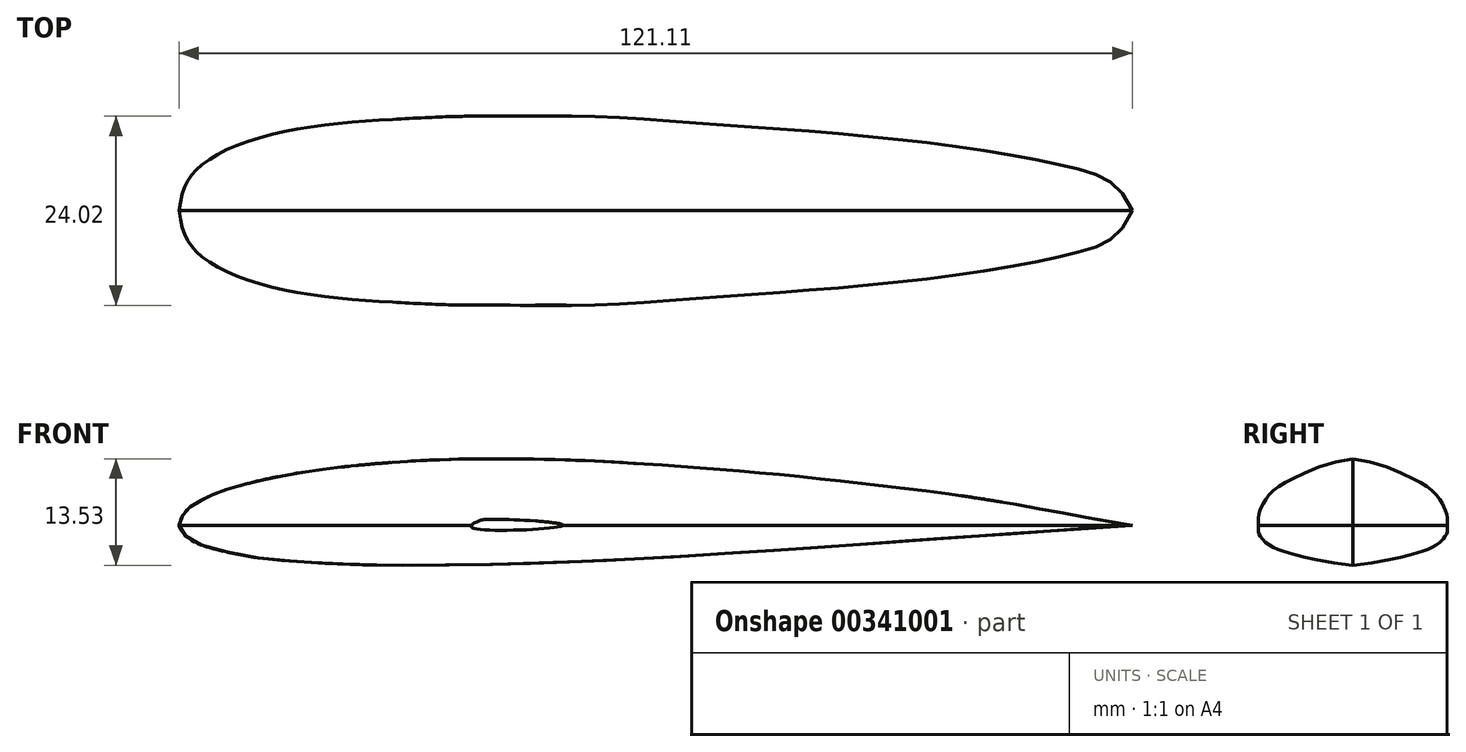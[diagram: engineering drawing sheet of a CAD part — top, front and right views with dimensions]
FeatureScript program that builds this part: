
annotation { "Feature Type Name" : "Feature", "Feature Type Description" : "" }
export const myFeature = defineFeature(function(context is Context, id is Id, definition is map)
    precondition{}
    {
        {
            var Q0;
            Q0=qCreatedBy(makeId("Front.planeOp"),FACE);
            var sketch = newSketch(context, id + "F0", { "sketchPlane" : qUnion([Q0])});
            skFitSpline(sketch, "E0", {"points": [v(-109.58, 0) * mm, v(-108.84, 1.66) * mm, v(-106.74, 3.18) * mm, v(-103.8, 4.43) * mm, v(-98.15, 5.93) * mm, v(-91.38, 7.1) * mm, v(-82.4, 7.99) * mm, v(-72.78, 8.41) * mm, v(-60.7, 8.3) * mm, v(-50.48, 7.79) * mm, v(-37.9, 6.86) * mm, v(-23.66, 5.4) * mm, v(-6.97, 3.25) * mm, v(11.53, 0) * mm], "startDerivative": vector(15.02, 46.78) * mm, "endDerivative": vector(165.18, -26.76) * mm});
            skLineSegment(sketch, "E1", {"start": v(11.53, 0) * mm, "end": v(11.53, 0) * mm});
            skFitSpline(sketch, "E2", {"points": [v(-109.58, 0) * mm, v(-109.4, -0.48) * mm, v(-108.4, -1.65) * mm, v(-106.45, -2.6) * mm, v(-101.35, -3.84) * mm, v(-95.03, -4.6) * mm, v(-86.91, -5) * mm, v(-76.49, -5.08) * mm, v(-63.19, -4.78) * mm, v(-51.7, -4.3) * mm, v(-35.91, -3.33) * mm, v(-24.18, -2.5) * mm, v(-10.17, -1.52) * mm, v(11.53, 0) * mm], "startDerivative": vector(4.26, -26.1) * mm, "endDerivative": vector(181.81, 12.76) * mm});
            skPoint(sketch, "E3", {"position": v(-109.56, 50.72) * mm});
            skSolve(sketch);
        }
        {
            var Q0;
            Q0=qCreatedBy(makeId("Front.planeOp"),FACE);
            cPlane(context, id + "F1", {"entities" : qUnion([Q0]), "cplaneType" : CPlaneType.OFFSET, "offset" : 12 * mm, "width" : 150 * mm, "height" : 150 * mm});
        }
        {
            var Q0;
            Q0=qCreatedBy(id+"F1.planeOp",FACE);
            var sketch = newSketch(context, id + "F2", { "sketchPlane" : qUnion([Q0])});
            skFitSpline(sketch, "E4", {"points": [v(-70.05, 0.77) * mm, v(-71.57, 0.5) * mm, v(-72.41, 0) * mm, v(-71.78, -0.48) * mm, v(-60.78, 0) * mm, v(-70.05, 0.77) * mm]});
            skPoint(sketch, "E5", {"position": v(-67.2, 0.7) * mm});
            skPoint(sketch, "E6", {"position": v(-64.3, 0.53) * mm});
            skPoint(sketch, "E7", {"position": v(-69.51, -0.64) * mm});
            skPoint(sketch, "E8", {"position": v(-66.72, -0.62) * mm});
            skPoint(sketch, "E9", {"position": v(-63.78, -0.47) * mm});
            skPoint(sketch, "E10", {"position": v(-61.75, -0.26) * mm});
            skPoint(sketch, "E11", {"position": v(-61.99, 0.32) * mm});
            skPoint(sketch, "E12", {"position": v(-60.82, 0.06) * mm});
            skPoint(sketch, "E13", {"position": v(-60.82, -0.04) * mm});
            skSolve(sketch);
        }
        {
            var Q0;
            Q0=qCreatedBy(makeId("Top.planeOp"),FACE);
            var sketch = newSketch(context, id + "F3", { "sketchPlane" : qUnion([Q0])});
            skFitSpline(sketch, "E14", {"points": [v(-109.58, 0) * mm, v(-107.55, -5.01) * mm, v(-98.59, -9.5) * mm, v(-81.02, -11.7) * mm, v(-72.41, -12) * mm], "startDerivative": vector(6.08, -37.14) * mm, "endDerivative": vector(19.3, 0.26) * mm});
            skFitSpline(sketch, "E15", {"points": [v(11.53, 0) * mm, v(4.5, -5.32) * mm, v(-15.68, -8.78) * mm, v(-41.53, -11) * mm, v(-60.78, -12) * mm], "startDerivative": vector(-25.52, -62.57) * mm, "endDerivative": vector(-69.24, 0.83) * mm});
            skSolve(sketch);
        }
        {
            var Q0;
            Q0=makeQuery(id+"F0.imprint","IMPRINT",FACE,{"disambiguationData":[TD([[makeQuery(id+"F0.imprint","IMPRINT",EDGE,{"derivedFrom":sQuery(id+"F0.wireOp",EDGE,"E0")}),-1.0]])]});
            var Q1;
            Q1=makeQuery(id+"F2.imprint","IMPRINT",FACE,{"disambiguationData":[TD([[makeQuery(id+"F2.imprint","IMPRINT",EDGE,{"derivedFrom":sQuery(id+"F2.wireOp",EDGE,"E4")}),1.0]])]});
            var Q2;
            Q2=sQuery(id+"F3.wireOp",EDGE,"E14");
            var Q3;
            Q3=sQuery(id+"F3.wireOp",EDGE,"E15");
            var Q4;
            Q4=sQuery(id+"F2.wireOp",VERTEX,"E6");
            var Q5;
            Q5=sQuery(id+"F0.wireOp",VERTEX,"E0.9.internal");
            loft(context, id + "F4", {"addGuides" : true, "sheetProfilesArray" : [{ "sheetProfileEntities" : qUnion([Q0]) }, { "sheetProfileEntities" : qUnion([Q1]) }], "guidesArray" : [{ "guideEntities" : qUnion([Q2]), "guideDerivativeType" : LoftGuideDerivativeType.DEFAULT, "guideDerivativeMagnitude" : 1 }, { "guideEntities" : qUnion([Q3]), "guideDerivativeType" : LoftGuideDerivativeType.DEFAULT, "guideDerivativeMagnitude" : 1 }], "matchConnections" : true, "connections" : [{ "connectionEntities" : qUnion([Q4, Q5]), "connectionEdgeQueries" : qUnion([]), "connectionEdgeParameters" : [] }]});
        }
        {
            var Q0;
            Q0=makeQuery(id+"F4.opLoft","SWEPT_BODY",BODY,{"disambiguationData":[OSD([makeQuery(id+"F0.imprint","IMPRINT",FACE,{"disambiguationData":[TD([[makeQuery(id+"F0.imprint","IMPRINT",EDGE,{"derivedFrom":sQuery(id+"F0.wireOp",EDGE,"E0")}),-1.0]])]}),makeQuery(id+"F2.imprint","IMPRINT",FACE,{"disambiguationData":[TD([[makeQuery(id+"F2.imprint","IMPRINT",EDGE,{"derivedFrom":sQuery(id+"F2.wireOp",EDGE,"E4")}),1.0]])]}),sQuery(id+"F3.wireOp",EDGE,"E14"),sQuery(id+"F3.wireOp",EDGE,"E15")])]});
            var Q1;
            Q1=qCreatedBy(makeId("Front.planeOp"),FACE);
            mirror(context, id + "F5", {"entities" : qUnion([Q0]), "mirrorPlane" : qUnion([Q1])});
        }
    });
